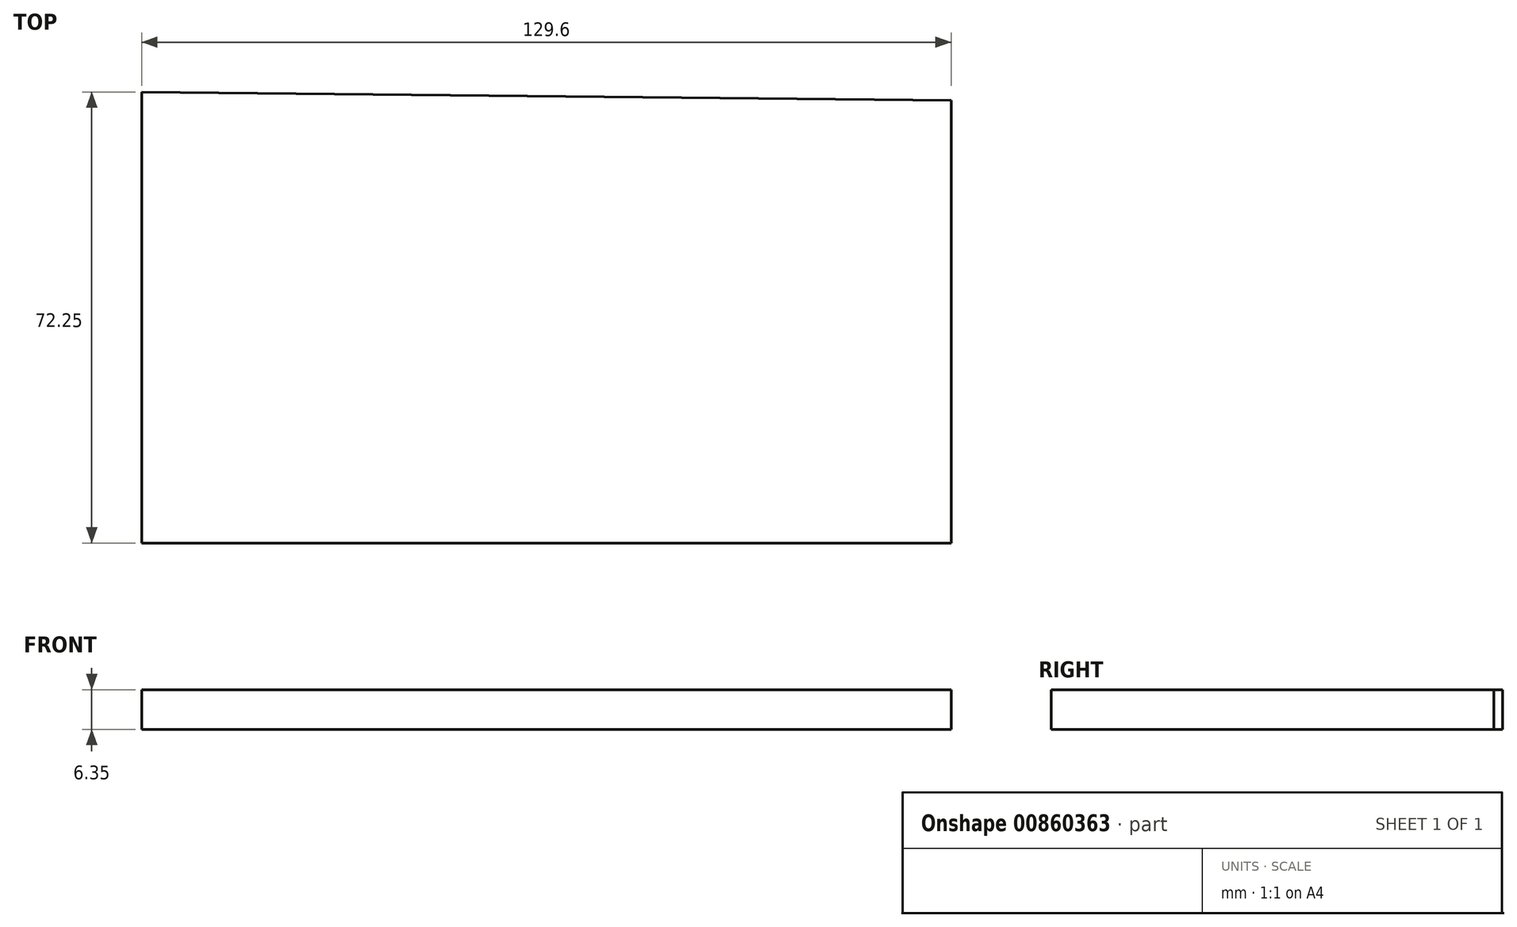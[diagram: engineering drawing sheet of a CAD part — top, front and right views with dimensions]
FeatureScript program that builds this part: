
annotation { "Feature Type Name" : "Feature", "Feature Type Description" : "" }
export const myFeature = defineFeature(function(context is Context, id is Id, definition is map)
    precondition{}
    {
        {
            var Q0;
            Q0=qCreatedBy(makeId("Top.planeOp"),FACE);
            var sketch = newSketch(context, id + "F0", { "sketchPlane" : qUnion([Q0])});
            skLineSegment(sketch, "E0", {"start": v(-65.16, -35.56) * mm, "end": v(-65.16, 36.7) * mm});
            skLineSegment(sketch, "E1", {"start": v(-65.16, -35.56) * mm, "end": v(64.44, -35.56) * mm});
            skLineSegment(sketch, "E2", {"start": v(64.44, -35.56) * mm, "end": v(64.44, 35.35) * mm});
            skLineSegment(sketch, "E3", {"start": v(64.44, 35.35) * mm, "end": v(-65.16, 36.7) * mm});
            skSolve(sketch);
        }
        {
            var Q0;
            Q0 = qSketchRegion(id + "F0", true);
            extrude(context, id + "F1", {"entities" : qUnion([Q0]), "depth" : 6.35 * mm, "offsetDistance" : 25.4 * mm});
        }
    });
